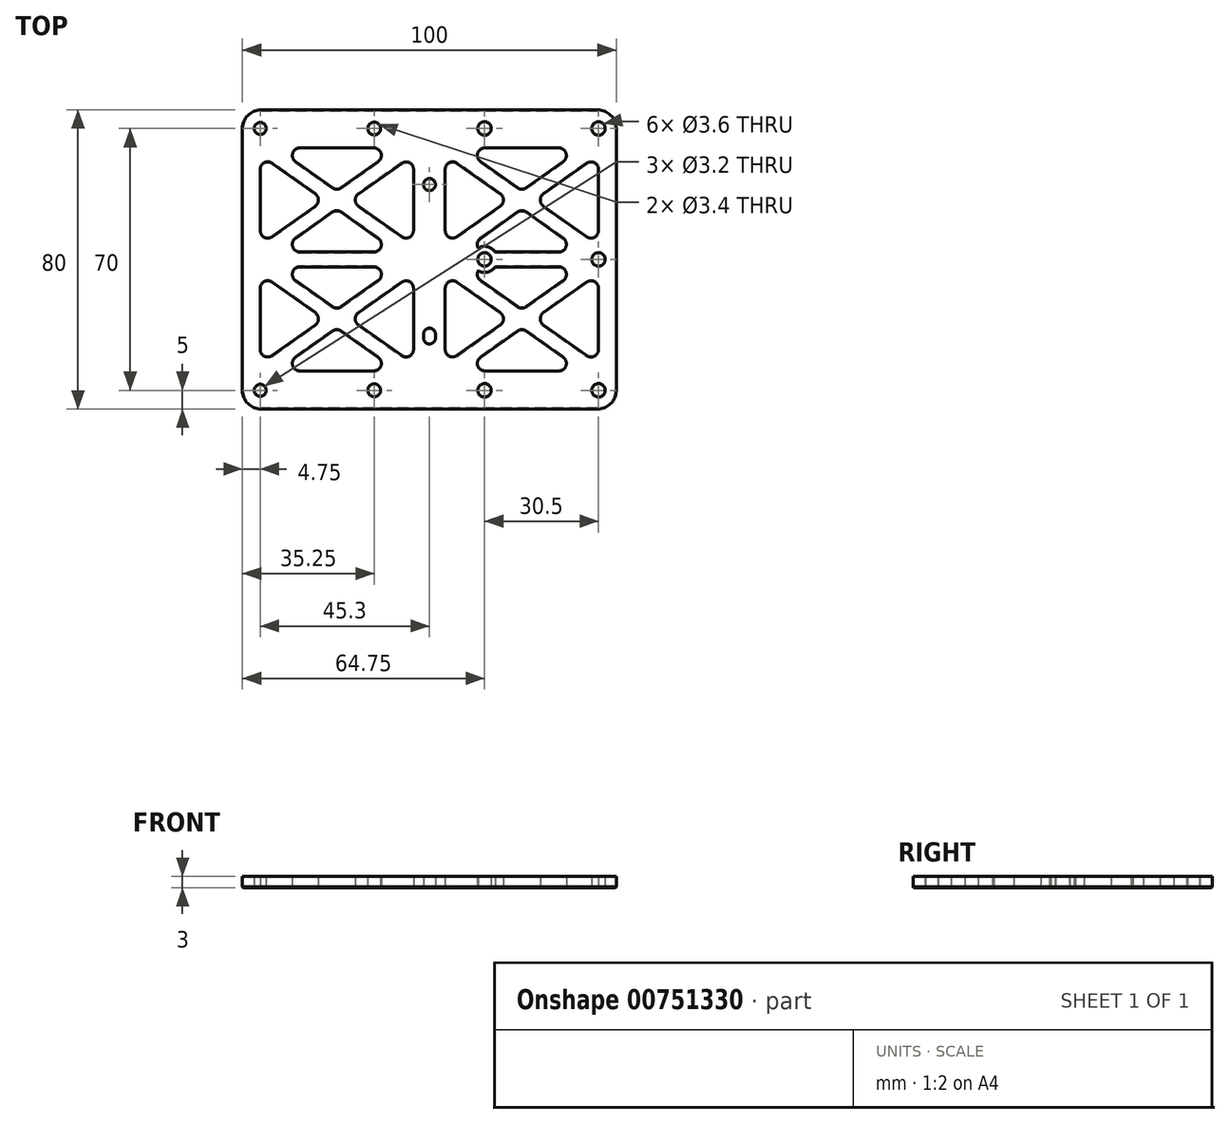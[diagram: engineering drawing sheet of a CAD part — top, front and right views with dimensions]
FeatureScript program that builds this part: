
annotation { "Feature Type Name" : "Feature", "Feature Type Description" : "" }
export const myFeature = defineFeature(function(context is Context, id is Id, definition is map)
    precondition{}
    {
        {
            var Q0;
            Q0=qCreatedBy(makeId("Top.planeOp"),FACE);
            var sketch = newSketch(context, id + "F0", { "sketchPlane" : qUnion([Q0])});
            skLineSegment(sketch, "E0", {"start": v(-45.25, 35) * mm, "end": v(-14.75, 35) * mm, "construction": true});
            skLineSegment(sketch, "E1.MirrorCS", {"start": v(-45.25, -35) * mm, "end": v(-14.75, -35) * mm, "construction": true});
            skLineSegment(sketch, "E2.MirrorCS", {"start": v(45.25, 35) * mm, "end": v(14.75, 35) * mm, "construction": true});
            skLineSegment(sketch, "E3.MirrorCS", {"start": v(45.25, -35) * mm, "end": v(14.75, -35) * mm, "construction": true});
            skPoint(sketch, "E4", {"position": v(-30, 35) * mm});
            skPoint(sketch, "E5", {"position": v(30, 35) * mm});
            skCircle(sketch, "E6", {"center": v(-45.25, 35) * mm, "radius": 1.5 * mm, "construction": true});
            skCircle(sketch, "E7", {"center": v(-14.75, 35) * mm, "radius": 1.5 * mm, "construction": true});
            skCircle(sketch, "E8.MirrorC", {"center": v(-45.25, -35) * mm, "radius": 1.5 * mm, "construction": true});
            skCircle(sketch, "E9.MirrorC", {"center": v(-14.75, -35) * mm, "radius": 1.5 * mm, "construction": true});
            skCircle(sketch, "E10.MirrorC", {"center": v(14.75, 35) * mm, "radius": 1.5 * mm, "construction": true});
            skCircle(sketch, "E11.MirrorC", {"center": v(45.25, 35) * mm, "radius": 1.5 * mm, "construction": true});
            skCircle(sketch, "E12.MirrorC", {"center": v(45.25, -35) * mm, "radius": 1.5 * mm, "construction": true});
            skCircle(sketch, "E13.MirrorC", {"center": v(14.75, -35) * mm, "radius": 1.5 * mm, "construction": true});
            skLineSegment(sketch, "E14", {"start": v(14.75, 0) * mm, "end": v(45.25, 0) * mm, "construction": true});
            skCircle(sketch, "E15", {"center": v(14.75, 0) * mm, "radius": 1.5 * mm, "construction": true});
            skCircle(sketch, "E16", {"center": v(45.25, 0) * mm, "radius": 1.5 * mm, "construction": true});
            skSolve(sketch);
        }
        {
            var Q0;
            Q0=qCreatedBy(makeId("Top.planeOp"),FACE);
            var sketch = newSketch(context, id + "F1", { "sketchPlane" : qUnion([Q0])});
            skLineSegment(sketch, "E17.bottom", {"start": v(50, 40) * mm, "end": v(-50, 40) * mm});
            skLineSegment(sketch, "E17.top", {"start": v(50, -40) * mm, "end": v(-50, -40) * mm});
            skLineSegment(sketch, "E17.left", {"start": v(50, 40) * mm, "end": v(50, -40) * mm});
            skLineSegment(sketch, "E17.right", {"start": v(-50, 40) * mm, "end": v(-50, -40) * mm});
            skCircle(sketch, "E18.0", {"center": v(-45.25, 35) * mm, "radius": 1.6 * mm});
            skCircle(sketch, "E19.0", {"center": v(-45.25, -35) * mm, "radius": 1.6 * mm});
            skCircle(sketch, "E20.0", {"center": v(-14.75, 35) * mm, "radius": 1.7 * mm});
            skCircle(sketch, "E21.0", {"center": v(-14.75, -35) * mm, "radius": 1.7 * mm});
            skCircle(sketch, "E22.0", {"center": v(14.75, 35) * mm, "radius": 1.8 * mm});
            skCircle(sketch, "E23.0", {"center": v(45.25, 35) * mm, "radius": 1.8 * mm});
            skCircle(sketch, "E24.0", {"center": v(14.75, -35) * mm, "radius": 1.8 * mm});
            skCircle(sketch, "E25.0", {"center": v(45.25, -35) * mm, "radius": 1.8 * mm});
            skLineSegment(sketch, "E26", {"start": v(0.05, 20) * mm, "end": v(0.05, -20) * mm, "construction": true});
            skCircle(sketch, "E27", {"center": v(0.05, 20) * mm, "radius": 1.6 * mm});
            skLineSegment(sketch, "E28", {"start": v(0.05, -20) * mm, "end": v(0.05, -21) * mm});
            skArc(sketch, "E29", {"start": v(-1.55, -20) * mm, "mid": v(0.05, -18.4) * mm, "end": v(1.65, -20) * mm});
            skArc(sketch, "E30", {"start": v(-1.55, -21) * mm, "mid": v(0.05, -22.6) * mm, "end": v(1.65, -21) * mm});
            skLineSegment(sketch, "E31", {"start": v(-1.55, -20) * mm, "end": v(-1.55, -21) * mm});
            skLineSegment(sketch, "E32", {"start": v(1.65, -20) * mm, "end": v(1.65, -21) * mm});
            skLineSegment(sketch, "E33.bottom", {"start": v(-2.24, 31.8) * mm, "end": v(-47.24, 31.8) * mm, "construction": true});
            skLineSegment(sketch, "E33.top", {"start": v(-2.24, 0) * mm, "end": v(-47.24, 0) * mm, "construction": true});
            skLineSegment(sketch, "E33.left", {"start": v(-2.24, 31.8) * mm, "end": v(-2.24, 0) * mm, "construction": true});
            skLineSegment(sketch, "E33.right", {"start": v(-47.24, 31.8) * mm, "end": v(-47.24, 0) * mm, "construction": true});
            skPoint(sketch, "E33.middle", {"position": v(-24.74, 15.9) * mm});
            skLineSegment(sketch, "E34", {"start": v(-24.74, 15.9) * mm, "end": v(-47.24, 31.8) * mm, "construction": true});
            skLineSegment(sketch, "E35", {"start": v(-24.74, 15.9) * mm, "end": v(-47.24, 0) * mm, "construction": true});
            skLineSegment(sketch, "E36", {"start": v(-24.74, 15.9) * mm, "end": v(-2.24, 0) * mm, "construction": true});
            skLineSegment(sketch, "E37", {"start": v(-2.24, 31.8) * mm, "end": v(-24.74, 15.9) * mm, "construction": true});
            skLineSegment(sketch, "E38.0", {"start": v(-8.54, 29.8) * mm, "end": v(-40.95, 29.8) * mm, "construction": true});
            skLineSegment(sketch, "E38.1", {"start": v(-8.54, 29.8) * mm, "end": v(-24.74, 18.35) * mm, "construction": true});
            skLineSegment(sketch, "E38.2", {"start": v(-24.74, 18.35) * mm, "end": v(-40.95, 29.8) * mm, "construction": true});
            skLineSegment(sketch, "E39.0", {"start": v(-28.2, 15.9) * mm, "end": v(-45.24, 27.94) * mm, "construction": true});
            skLineSegment(sketch, "E39.1", {"start": v(-28.2, 15.9) * mm, "end": v(-45.24, 3.86) * mm, "construction": true});
            skLineSegment(sketch, "E39.2", {"start": v(-45.24, 27.94) * mm, "end": v(-45.24, 3.86) * mm, "construction": true});
            skLineSegment(sketch, "E40.0", {"start": v(-24.74, 13.45) * mm, "end": v(-40.95, 2) * mm, "construction": true});
            skLineSegment(sketch, "E40.1", {"start": v(-24.74, 13.45) * mm, "end": v(-8.54, 2) * mm, "construction": true});
            skLineSegment(sketch, "E40.2", {"start": v(-8.54, 2) * mm, "end": v(-40.95, 2) * mm, "construction": true});
            skLineSegment(sketch, "E41.0", {"start": v(-4.24, 27.94) * mm, "end": v(-4.24, 3.86) * mm, "construction": true});
            skLineSegment(sketch, "E41.1", {"start": v(-4.24, 27.94) * mm, "end": v(-21.28, 15.9) * mm, "construction": true});
            skLineSegment(sketch, "E41.2", {"start": v(-21.28, 15.9) * mm, "end": v(-4.24, 3.86) * mm, "construction": true});
            skCircle(sketch, "E42.0", {"center": v(14.75, 0) * mm, "radius": 1.8 * mm});
            skCircle(sketch, "E43.0", {"center": v(45.25, 0) * mm, "radius": 1.8 * mm});
            skSolve(sketch);
        }
        {
            var Q0;
            Q0 = qSketchRegion(id + "F1", true);
            extrude(context, id + "F2", {"entities" : qUnion([Q0]), "depth" : 3 * mm, "offsetDistance" : 25 * mm});
        }
        {
            var Q0;
            Q0=qCreatedBy(makeId("Top.planeOp"),FACE);
            var sketch = newSketch(context, id + "F3", { "sketchPlane" : qUnion([Q0])});
            skLineSegment(sketch, "E44.0", {"start": v(-30.52, 17.53) * mm, "end": v(-42.09, 25.71) * mm});
            skLineSegment(sketch, "E45.0", {"start": v(-45.24, 24.08) * mm, "end": v(-45.24, 7.72) * mm});
            skLineSegment(sketch, "E46.0", {"start": v(-30.52, 14.27) * mm, "end": v(-42.09, 6.1) * mm});
            skLineSegment(sketch, "E47.0", {"start": v(-25.9, 12.64) * mm, "end": v(-35.8, 5.63) * mm});
            skLineSegment(sketch, "E48.0", {"start": v(-14.83, 2) * mm, "end": v(-34.65, 2) * mm});
            skLineSegment(sketch, "E49.0", {"start": v(-23.59, 12.64) * mm, "end": v(-13.68, 5.63) * mm});
            skLineSegment(sketch, "E50.0", {"start": v(-18.97, 14.27) * mm, "end": v(-7.4, 6.1) * mm});
            skLineSegment(sketch, "E51.0", {"start": v(-7.4, 25.71) * mm, "end": v(-18.97, 17.53) * mm});
            skLineSegment(sketch, "E52.0", {"start": v(-4.24, 24.08) * mm, "end": v(-4.24, 7.72) * mm});
            skLineSegment(sketch, "E53.0", {"start": v(-14.83, 29.8) * mm, "end": v(-34.65, 29.8) * mm});
            skLineSegment(sketch, "E54.0", {"start": v(-13.68, 26.17) * mm, "end": v(-23.59, 19.17) * mm});
            skLineSegment(sketch, "E55.0", {"start": v(-25.9, 19.17) * mm, "end": v(-35.8, 26.17) * mm});
            skPoint(sketch, "E56.visualSharp", {"position": v(-40.95, 29.8) * mm});
            skArc(sketch, "E56.filletArc", {"start": v(-34.65, 29.8) * mm, "mid": v(-36.56, 28.4) * mm, "end": v(-35.8, 26.17) * mm});
            skPoint(sketch, "E57.visualSharp", {"position": v(-8.54, 29.8) * mm});
            skArc(sketch, "E57.filletArc", {"start": v(-13.68, 26.17) * mm, "mid": v(-12.93, 28.4) * mm, "end": v(-14.83, 29.8) * mm});
            skPoint(sketch, "E58.visualSharp", {"position": v(-24.74, 18.35) * mm});
            skArc(sketch, "E58.filletArc", {"start": v(-25.9, 19.17) * mm, "mid": v(-24.74, 18.8) * mm, "end": v(-23.59, 19.17) * mm});
            skPoint(sketch, "E59.visualSharp", {"position": v(-45.24, 27.94) * mm});
            skArc(sketch, "E59.filletArc", {"start": v(-42.09, 25.71) * mm, "mid": v(-44.16, 25.85) * mm, "end": v(-45.24, 24.08) * mm});
            skPoint(sketch, "E60.visualSharp", {"position": v(-45.24, 3.86) * mm});
            skArc(sketch, "E60.filletArc", {"start": v(-45.24, 7.72) * mm, "mid": v(-44.16, 5.95) * mm, "end": v(-42.09, 6.1) * mm});
            skPoint(sketch, "E61.visualSharp", {"position": v(-28.2, 15.9) * mm});
            skArc(sketch, "E61.filletArc", {"start": v(-30.52, 14.27) * mm, "mid": v(-29.67, 15.9) * mm, "end": v(-30.52, 17.53) * mm});
            skPoint(sketch, "E62.visualSharp", {"position": v(-24.74, 13.45) * mm});
            skArc(sketch, "E62.filletArc", {"start": v(-23.59, 12.64) * mm, "mid": v(-24.74, 13) * mm, "end": v(-25.9, 12.64) * mm});
            skPoint(sketch, "E63.visualSharp", {"position": v(-40.95, 2) * mm});
            skArc(sketch, "E63.filletArc", {"start": v(-35.8, 5.63) * mm, "mid": v(-36.56, 3.4) * mm, "end": v(-34.65, 2) * mm});
            skPoint(sketch, "E64.visualSharp", {"position": v(-8.54, 2) * mm});
            skArc(sketch, "E64.filletArc", {"start": v(-14.83, 2) * mm, "mid": v(-12.93, 3.4) * mm, "end": v(-13.68, 5.63) * mm});
            skPoint(sketch, "E65.visualSharp", {"position": v(-21.28, 15.9) * mm});
            skArc(sketch, "E65.filletArc", {"start": v(-18.97, 17.53) * mm, "mid": v(-19.81, 15.9) * mm, "end": v(-18.97, 14.27) * mm});
            skPoint(sketch, "E66.visualSharp", {"position": v(-4.24, 27.94) * mm});
            skArc(sketch, "E66.filletArc", {"start": v(-4.24, 24.08) * mm, "mid": v(-5.32, 25.85) * mm, "end": v(-7.4, 25.71) * mm});
            skPoint(sketch, "E67.visualSharp", {"position": v(-4.24, 3.86) * mm});
            skArc(sketch, "E67.filletArc", {"start": v(-7.4, 6.1) * mm, "mid": v(-5.32, 5.95) * mm, "end": v(-4.24, 7.72) * mm});
            skArc(sketch, "E68.MirrorCS", {"start": v(23.59, 12.64) * mm, "mid": v(24.74, 13) * mm, "end": v(25.9, 12.64) * mm});
            skArc(sketch, "E69.MirrorCS", {"start": v(30.52, 14.27) * mm, "mid": v(29.67, 15.9) * mm, "end": v(30.52, 17.53) * mm});
            skPoint(sketch, "E70.MirrorP", {"position": v(24.74, 13.45) * mm});
            skArc(sketch, "E71.MirrorCS", {"start": v(18.97, 17.53) * mm, "mid": v(19.81, 15.9) * mm, "end": v(18.97, 14.27) * mm});
            skArc(sketch, "E72.MirrorCS", {"start": v(25.9, 19.17) * mm, "mid": v(24.74, 18.8) * mm, "end": v(23.59, 19.17) * mm});
            skPoint(sketch, "E73.MirrorP", {"position": v(28.2, 15.9) * mm});
            skArc(sketch, "E74.MirrorCS", {"start": v(13.68, 26.17) * mm, "mid": v(12.93, 28.4) * mm, "end": v(14.83, 29.8) * mm});
            skArc(sketch, "E75.MirrorCS", {"start": v(45.24, 7.72) * mm, "mid": v(44.16, 5.95) * mm, "end": v(42.09, 6.1) * mm});
            skArc(sketch, "E76.MirrorCS", {"start": v(14.83, 2) * mm, "mid": v(12.93, 3.4) * mm, "end": v(13.68, 5.63) * mm});
            skArc(sketch, "E77.MirrorCS", {"start": v(7.4, 6.1) * mm, "mid": v(5.32, 5.95) * mm, "end": v(4.24, 7.72) * mm});
            skArc(sketch, "E78.MirrorCS", {"start": v(35.8, 5.63) * mm, "mid": v(36.56, 3.4) * mm, "end": v(34.65, 2) * mm});
            skArc(sketch, "E79.MirrorCS", {"start": v(42.09, 25.71) * mm, "mid": v(44.16, 25.85) * mm, "end": v(45.24, 24.08) * mm});
            skPoint(sketch, "E80.MirrorP", {"position": v(21.28, 15.9) * mm});
            skArc(sketch, "E81.MirrorCS", {"start": v(4.24, 24.08) * mm, "mid": v(5.32, 25.85) * mm, "end": v(7.4, 25.71) * mm});
            skArc(sketch, "E82.MirrorCS", {"start": v(34.65, 29.8) * mm, "mid": v(36.56, 28.4) * mm, "end": v(35.8, 26.17) * mm});
            skLineSegment(sketch, "E83.MirrorCS", {"start": v(7.4, 25.71) * mm, "end": v(18.97, 17.53) * mm});
            skLineSegment(sketch, "E84.MirrorCS", {"start": v(13.68, 26.17) * mm, "end": v(23.59, 19.17) * mm});
            skPoint(sketch, "E85.MirrorP", {"position": v(40.95, 2) * mm});
            skLineSegment(sketch, "E86.MirrorCS", {"start": v(4.24, 24.08) * mm, "end": v(4.24, 7.72) * mm});
            skLineSegment(sketch, "E87.MirrorCS", {"start": v(14.83, 2) * mm, "end": v(34.65, 2) * mm});
            skLineSegment(sketch, "E88.MirrorCS", {"start": v(14.83, 29.8) * mm, "end": v(34.65, 29.8) * mm});
            skLineSegment(sketch, "E89.MirrorCS", {"start": v(18.97, 14.27) * mm, "end": v(7.4, 6.1) * mm});
            skLineSegment(sketch, "E90.MirrorCS", {"start": v(30.52, 17.53) * mm, "end": v(42.09, 25.71) * mm});
            skLineSegment(sketch, "E91.MirrorCS", {"start": v(30.52, 14.27) * mm, "end": v(42.09, 6.1) * mm});
            skLineSegment(sketch, "E92.MirrorCS", {"start": v(45.24, 24.08) * mm, "end": v(45.24, 7.72) * mm});
            skLineSegment(sketch, "E93.MirrorCS", {"start": v(23.59, 12.64) * mm, "end": v(13.68, 5.63) * mm});
            skPoint(sketch, "E94.MirrorP", {"position": v(8.54, 29.8) * mm});
            skPoint(sketch, "E95.MirrorP", {"position": v(8.54, 2) * mm});
            skPoint(sketch, "E96.MirrorP", {"position": v(24.74, 18.35) * mm});
            skLineSegment(sketch, "E97.MirrorCS", {"start": v(25.9, 19.17) * mm, "end": v(35.8, 26.17) * mm});
            skPoint(sketch, "E98.MirrorP", {"position": v(45.24, 3.86) * mm});
            skPoint(sketch, "E99.MirrorP", {"position": v(4.24, 27.94) * mm});
            skLineSegment(sketch, "E100.MirrorCS", {"start": v(25.9, 12.64) * mm, "end": v(35.8, 5.63) * mm});
            skPoint(sketch, "E101.MirrorP", {"position": v(45.24, 27.94) * mm});
            skPoint(sketch, "E102.MirrorP", {"position": v(40.95, 29.8) * mm});
            skPoint(sketch, "E103.MirrorP", {"position": v(4.24, 3.86) * mm});
            skArc(sketch, "E104.MirrorCS", {"start": v(25.9, -19.17) * mm, "mid": v(24.74, -18.8) * mm, "end": v(23.59, -19.17) * mm});
            skArc(sketch, "E105.MirrorCS", {"start": v(-18.97, -17.53) * mm, "mid": v(-19.81, -15.9) * mm, "end": v(-18.97, -14.27) * mm});
            skArc(sketch, "E106.MirrorCS", {"start": v(18.97, -17.53) * mm, "mid": v(19.81, -15.9) * mm, "end": v(18.97, -14.27) * mm});
            skPoint(sketch, "E107.MirrorP", {"position": v(24.74, -18.35) * mm});
            skArc(sketch, "E108.MirrorCS", {"start": v(7.4, -6.1) * mm, "mid": v(5.32, -5.95) * mm, "end": v(4.24, -7.72) * mm});
            skArc(sketch, "E109.MirrorCS", {"start": v(-45.24, -7.72) * mm, "mid": v(-44.16, -5.95) * mm, "end": v(-42.09, -6.1) * mm});
            skArc(sketch, "E110.MirrorCS", {"start": v(-25.9, -19.17) * mm, "mid": v(-24.74, -18.8) * mm, "end": v(-23.59, -19.17) * mm});
            skArc(sketch, "E111.MirrorCS", {"start": v(-13.68, -26.17) * mm, "mid": v(-12.93, -28.4) * mm, "end": v(-14.83, -29.8) * mm});
            skArc(sketch, "E112.MirrorCS", {"start": v(-23.59, -12.64) * mm, "mid": v(-24.74, -13) * mm, "end": v(-25.9, -12.64) * mm});
            skArc(sketch, "E113.MirrorCS", {"start": v(30.52, -14.27) * mm, "mid": v(29.67, -15.9) * mm, "end": v(30.52, -17.53) * mm});
            skArc(sketch, "E114.MirrorCS", {"start": v(23.59, -12.64) * mm, "mid": v(24.74, -13) * mm, "end": v(25.9, -12.64) * mm});
            skArc(sketch, "E115.MirrorCS", {"start": v(-30.52, -14.27) * mm, "mid": v(-29.67, -15.9) * mm, "end": v(-30.52, -17.53) * mm});
            skArc(sketch, "E116.MirrorCS", {"start": v(45.24, -7.72) * mm, "mid": v(44.16, -5.95) * mm, "end": v(42.09, -6.1) * mm});
            skArc(sketch, "E117.MirrorCS", {"start": v(-34.65, -29.8) * mm, "mid": v(-36.56, -28.4) * mm, "end": v(-35.8, -26.17) * mm});
            skArc(sketch, "E118.MirrorCS", {"start": v(42.09, -25.71) * mm, "mid": v(44.16, -25.85) * mm, "end": v(45.24, -24.08) * mm});
            skArc(sketch, "E119.MirrorCS", {"start": v(-14.83, -2) * mm, "mid": v(-12.93, -3.4) * mm, "end": v(-13.68, -5.63) * mm});
            skPoint(sketch, "E120.MirrorP", {"position": v(-24.74, -13.45) * mm});
            skPoint(sketch, "E121.MirrorP", {"position": v(24.74, -13.45) * mm});
            skArc(sketch, "E122.MirrorCS", {"start": v(4.24, -24.08) * mm, "mid": v(5.32, -25.85) * mm, "end": v(7.4, -25.71) * mm});
            skArc(sketch, "E123.MirrorCS", {"start": v(-7.4, -6.1) * mm, "mid": v(-5.32, -5.95) * mm, "end": v(-4.24, -7.72) * mm});
            skArc(sketch, "E124.MirrorCS", {"start": v(-42.09, -25.71) * mm, "mid": v(-44.16, -25.85) * mm, "end": v(-45.24, -24.08) * mm});
            skArc(sketch, "E125.MirrorCS", {"start": v(-4.24, -24.08) * mm, "mid": v(-5.32, -25.85) * mm, "end": v(-7.4, -25.71) * mm});
            skArc(sketch, "E126.MirrorCS", {"start": v(-35.8, -5.63) * mm, "mid": v(-36.56, -3.4) * mm, "end": v(-34.65, -2) * mm});
            skPoint(sketch, "E127.MirrorP", {"position": v(45.24, -3.86) * mm});
            skPoint(sketch, "E128.MirrorP", {"position": v(4.24, -27.94) * mm});
            skPoint(sketch, "E129.MirrorP", {"position": v(-24.74, -18.35) * mm});
            skLineSegment(sketch, "E130.MirrorCS", {"start": v(18.97, -14.27) * mm, "end": v(7.4, -6.1) * mm});
            skLineSegment(sketch, "E131.MirrorCS", {"start": v(-14.83, -29.8) * mm, "end": v(-34.65, -29.8) * mm});
            skLineSegment(sketch, "E132.MirrorCS", {"start": v(7.4, -25.71) * mm, "end": v(18.97, -17.53) * mm});
            skLineSegment(sketch, "E133.MirrorCS", {"start": v(-30.52, -14.27) * mm, "end": v(-42.09, -6.1) * mm});
            skLineSegment(sketch, "E134.MirrorCS", {"start": v(14.83, -2) * mm, "end": v(34.65, -2) * mm});
            skLineSegment(sketch, "E135.MirrorCS", {"start": v(-4.24, -24.08) * mm, "end": v(-4.24, -7.72) * mm});
            skLineSegment(sketch, "E136.MirrorCS", {"start": v(-7.4, -25.71) * mm, "end": v(-18.97, -17.53) * mm});
            skLineSegment(sketch, "E137.MirrorCS", {"start": v(25.9, -12.64) * mm, "end": v(35.8, -5.63) * mm});
            skPoint(sketch, "E138.MirrorP", {"position": v(-21.28, -15.9) * mm});
            skArc(sketch, "E139.MirrorCS", {"start": v(14.83, -2) * mm, "mid": v(12.93, -3.4) * mm, "end": v(13.68, -5.63) * mm});
            skLineSegment(sketch, "E140.MirrorCS", {"start": v(30.52, -14.27) * mm, "end": v(42.09, -6.1) * mm});
            skArc(sketch, "E141.MirrorCS", {"start": v(34.65, -29.8) * mm, "mid": v(36.56, -28.4) * mm, "end": v(35.8, -26.17) * mm});
            skPoint(sketch, "E142.MirrorP", {"position": v(-4.24, -3.86) * mm});
            skPoint(sketch, "E143.MirrorP", {"position": v(-40.95, -29.8) * mm});
            skPoint(sketch, "E144.MirrorP", {"position": v(28.2, -15.9) * mm});
            skPoint(sketch, "E145.MirrorP", {"position": v(4.24, -3.86) * mm});
            skLineSegment(sketch, "E146.MirrorCS", {"start": v(-30.52, -17.53) * mm, "end": v(-42.09, -25.71) * mm});
            skPoint(sketch, "E147.MirrorP", {"position": v(21.28, -15.9) * mm});
            skLineSegment(sketch, "E148.MirrorCS", {"start": v(-45.24, -24.08) * mm, "end": v(-45.24, -7.72) * mm});
            skLineSegment(sketch, "E149.MirrorCS", {"start": v(-25.9, -19.17) * mm, "end": v(-35.8, -26.17) * mm});
            skLineSegment(sketch, "E150.MirrorCS", {"start": v(-23.59, -12.64) * mm, "end": v(-13.68, -5.63) * mm});
            skLineSegment(sketch, "E151.MirrorCS", {"start": v(13.68, -26.17) * mm, "end": v(23.59, -19.17) * mm});
            skLineSegment(sketch, "E152.MirrorCS", {"start": v(45.24, -24.08) * mm, "end": v(45.24, -7.72) * mm});
            skLineSegment(sketch, "E153.MirrorCS", {"start": v(-18.97, -14.27) * mm, "end": v(-7.4, -6.1) * mm});
            skLineSegment(sketch, "E154.MirrorCS", {"start": v(-13.68, -26.17) * mm, "end": v(-23.59, -19.17) * mm});
            skLineSegment(sketch, "E155.MirrorCS", {"start": v(30.52, -17.53) * mm, "end": v(42.09, -25.71) * mm});
            skLineSegment(sketch, "E156.MirrorCS", {"start": v(23.59, -12.64) * mm, "end": v(13.68, -5.63) * mm});
            skLineSegment(sketch, "E157.MirrorCS", {"start": v(14.83, -29.8) * mm, "end": v(34.65, -29.8) * mm});
            skArc(sketch, "E158.MirrorCS", {"start": v(13.68, -26.17) * mm, "mid": v(12.93, -28.4) * mm, "end": v(14.83, -29.8) * mm});
            skPoint(sketch, "E159.MirrorP", {"position": v(40.95, -2) * mm});
            skPoint(sketch, "E160.MirrorP", {"position": v(8.54, -2) * mm});
            skPoint(sketch, "E161.MirrorP", {"position": v(-40.95, -2) * mm});
            skPoint(sketch, "E162.MirrorP", {"position": v(-45.24, -27.94) * mm});
            skPoint(sketch, "E163.MirrorP", {"position": v(-45.24, -3.86) * mm});
            skPoint(sketch, "E164.MirrorP", {"position": v(-8.54, -29.8) * mm});
            skLineSegment(sketch, "E165.MirrorCS", {"start": v(-25.9, -12.64) * mm, "end": v(-35.8, -5.63) * mm});
            skPoint(sketch, "E166.MirrorP", {"position": v(-28.2, -15.9) * mm});
            skLineSegment(sketch, "E167.MirrorCS", {"start": v(-14.83, -2) * mm, "end": v(-34.65, -2) * mm});
            skPoint(sketch, "E168.MirrorP", {"position": v(-8.54, -2) * mm});
            skArc(sketch, "E169.MirrorCS", {"start": v(35.8, -5.63) * mm, "mid": v(36.56, -3.4) * mm, "end": v(34.65, -2) * mm});
            skLineSegment(sketch, "E170.MirrorCS", {"start": v(25.9, -19.17) * mm, "end": v(35.8, -26.17) * mm});
            skPoint(sketch, "E171.MirrorP", {"position": v(8.54, -29.8) * mm});
            skPoint(sketch, "E172.MirrorP", {"position": v(45.24, -27.94) * mm});
            skLineSegment(sketch, "E173.MirrorCS", {"start": v(4.24, -24.08) * mm, "end": v(4.24, -7.72) * mm});
            skPoint(sketch, "E174.MirrorP", {"position": v(-4.24, -27.94) * mm});
            skPoint(sketch, "E175.MirrorP", {"position": v(40.95, -29.8) * mm});
            skSolve(sketch);
        }
        {
            var Q0;
            Q0 = qSketchRegion(id + "F3", true);
            extrude(context, id + "F4", {"entities" : qUnion([Q0]), "operationType" : NewBodyOperationType.REMOVE, "endBound" : BoundingType.THROUGH_ALL, "depth" : 25 * mm, "offsetDistance" : 25 * mm});
        }
        {
            var Q0;
            Q0=qCreatedBy(makeId("Top.planeOp"),FACE);
            var sketch = newSketch(context, id + "F5", { "sketchPlane" : qUnion([Q0])});
            skCircle(sketch, "E176.0", {"center": v(14.75, 0) * mm, "radius": 1.8 * mm});
            skCircle(sketch, "E177", {"center": v(14.75, 0) * mm, "radius": 3.5 * mm});
            skSolve(sketch);
        }
        {
            var Q0;
            Q0 = qSketchRegion(id + "F5", true);
            var Q1;
            Q1=makeQuery(id+"F2.opExtrude","CAP_FACE",FACE,{"disambiguationData":[OSD([sQuery(id+"F1.wireOp",EDGE,"E17.bottom"),sQuery(id+"F1.wireOp",EDGE,"E17.top"),sQuery(id+"F1.wireOp",EDGE,"E17.left"),sQuery(id+"F1.wireOp",EDGE,"E17.right"),sQuery(id+"F1.wireOp",EDGE,"E18.0"),sQuery(id+"F1.wireOp",EDGE,"E19.0"),sQuery(id+"F1.wireOp",EDGE,"E20.0"),sQuery(id+"F1.wireOp",EDGE,"E21.0"),sQuery(id+"F1.wireOp",EDGE,"E22.0"),sQuery(id+"F1.wireOp",EDGE,"E23.0"),sQuery(id+"F1.wireOp",EDGE,"E24.0"),sQuery(id+"F1.wireOp",EDGE,"E25.0"),sQuery(id+"F1.wireOp",EDGE,"E27"),sQuery(id+"F1.wireOp",EDGE,"E29"),sQuery(id+"F1.wireOp",EDGE,"E30"),sQuery(id+"F1.wireOp",EDGE,"E31"),sQuery(id+"F1.wireOp",EDGE,"E32"),sQuery(id+"F1.wireOp",EDGE,"E42.0"),sQuery(id+"F1.wireOp",EDGE,"E43.0")])],"isStart":false});
            extrude(context, id + "F6", {"entities" : qUnion([Q0]), "operationType" : NewBodyOperationType.ADD, "endBound" : BoundingType.UP_TO_SURFACE, "depth" : 25 * mm, "endBoundEntityFace" : qUnion([Q1]), "offsetDistance" : 25 * mm});
        }
        {
            var Q0;
            Q0=makeQuery(id+"F2.opExtrude","SWEPT_EDGE",EDGE,{"disambiguationData":[OSD([sQuery(id+"F1.wireOp",EDGE,"E17.top"),sQuery(id+"F1.wireOp",EDGE,"E17.left")])]});
            var Q1;
            Q1=makeQuery(id+"F2.opExtrude","SWEPT_EDGE",EDGE,{"disambiguationData":[OSD([sQuery(id+"F1.wireOp",EDGE,"E17.bottom"),sQuery(id+"F1.wireOp",EDGE,"E17.left")])]});
            var Q2;
            Q2=makeQuery(id+"F2.opExtrude","SWEPT_EDGE",EDGE,{"disambiguationData":[OSD([sQuery(id+"F1.wireOp",EDGE,"E17.top"),sQuery(id+"F1.wireOp",EDGE,"E17.right")])]});
            var Q3;
            Q3=makeQuery(id+"F2.opExtrude","SWEPT_EDGE",EDGE,{"disambiguationData":[OSD([sQuery(id+"F1.wireOp",EDGE,"E17.bottom"),sQuery(id+"F1.wireOp",EDGE,"E17.right")])]});
            fillet(context, id + "F7", {"entities" : qUnion([Q0, Q1, Q2, Q3]), "radius" : 5 * mm, "allowEdgeOverflow" : false});
        }
        {
            var Q0;
            Q0=makeQuery(id+"F6.boolean.opBoolean","MERGE",FACE,{"derivedFrom":[makeQuery(id+"F2.opExtrude","CAP_FACE",FACE,{"disambiguationData":[OSD([sQuery(id+"F1.wireOp",EDGE,"E17.bottom"),sQuery(id+"F1.wireOp",EDGE,"E17.top"),sQuery(id+"F1.wireOp",EDGE,"E17.left"),sQuery(id+"F1.wireOp",EDGE,"E17.right"),sQuery(id+"F1.wireOp",EDGE,"E18.0"),sQuery(id+"F1.wireOp",EDGE,"E19.0"),sQuery(id+"F1.wireOp",EDGE,"E20.0"),sQuery(id+"F1.wireOp",EDGE,"E21.0"),sQuery(id+"F1.wireOp",EDGE,"E22.0"),sQuery(id+"F1.wireOp",EDGE,"E23.0"),sQuery(id+"F1.wireOp",EDGE,"E24.0"),sQuery(id+"F1.wireOp",EDGE,"E25.0"),sQuery(id+"F1.wireOp",EDGE,"E27"),sQuery(id+"F1.wireOp",EDGE,"E29"),sQuery(id+"F1.wireOp",EDGE,"E30"),sQuery(id+"F1.wireOp",EDGE,"E31"),sQuery(id+"F1.wireOp",EDGE,"E32"),sQuery(id+"F1.wireOp",EDGE,"E42.0"),sQuery(id+"F1.wireOp",EDGE,"E43.0")])],"isStart":true}),makeQuery(id+"F6.opExtrude","CAP_FACE",FACE,{"disambiguationData":[OSD([sQuery(id+"F5.wireOp",EDGE,"E176.0"),sQuery(id+"F5.wireOp",EDGE,"E177")])],"isStart":true})]});
            chamfer(context, id + "F8", {"entities" : qUnion([Q0]), "width" : 0.2 * mm});
        }
    });
